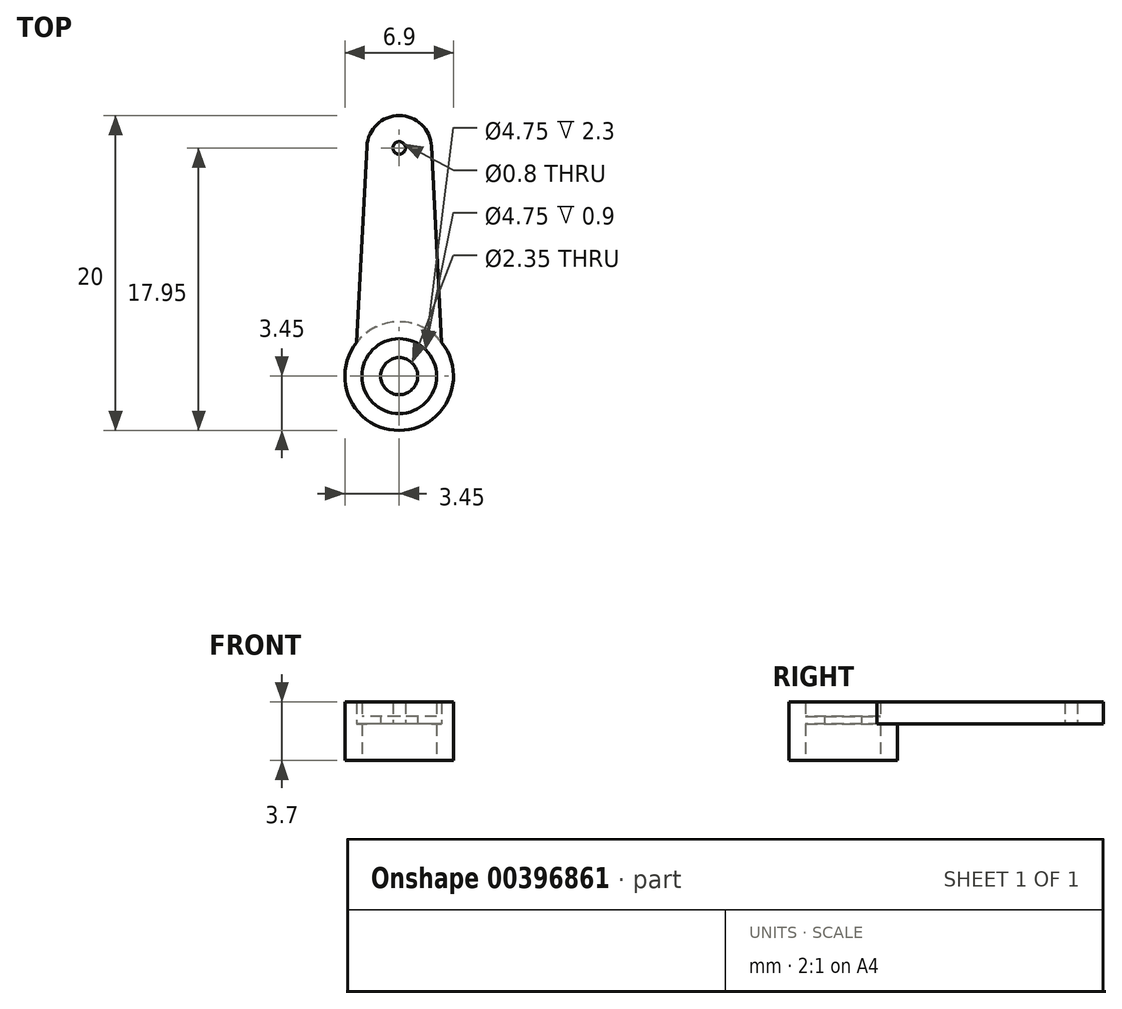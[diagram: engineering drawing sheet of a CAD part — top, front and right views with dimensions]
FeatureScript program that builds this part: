
annotation { "Feature Type Name" : "Feature", "Feature Type Description" : "" }
export const myFeature = defineFeature(function(context is Context, id is Id, definition is map)
    precondition{}
    {
        {
            var Q0;
            Q0=qCreatedBy(makeId("Top.planeOp"),FACE);
            var sketch = newSketch(context, id + "F0", { "sketchPlane" : qUnion([Q0])});
            skCircle(sketch, "E0", {"center": v(0, 0) * mm, "radius": 3.45 * mm});
            skCircle(sketch, "E1", {"center": v(0, 0) * mm, "radius": 2.38 * mm});
            skCircle(sketch, "E2", {"center": v(0, 0) * mm, "radius": 1.18 * mm});
            skCircle(sketch, "E3", {"center": v(0, 14.5) * mm, "radius": 0.4 * mm});
            skCircle(sketch, "E4", {"center": v(0, 14.5) * mm, "radius": 2.05 * mm});
            skLineSegment(sketch, "E5", {"start": v(-2.7, 2.15) * mm, "end": v(-2.05, 14.6) * mm});
            skLineSegment(sketch, "E6", {"start": v(2.05, 14.6) * mm, "end": v(2.7, 2.15) * mm});
            skLineSegment(sketch, "E7", {"start": v(-2.7, 2.15) * mm, "end": v(2.7, 2.15) * mm});
            skLineSegment(sketch, "E8", {"start": v(0, 2.15) * mm, "end": v(0, 0) * mm});
            skSolve(sketch);
        }
        {
            var Q0;
            Q0 = qSketchRegion(id + "F0", true);
            extrude(context, id + "F1", {"entities" : qUnion([Q0]), "depth" : 1.4 * mm});
        }
        {
            var Q0;
            {var subQ0=sQuery(id+"F0.wireOp",EDGE,"E7");var subQ4=sQuery(id+"F0.wireOp",EDGE,"E1");var subQ5=makeQuery(id+"F0.imprint","INTERSECT",VERTEX,{"disambiguationData":[OD(0.0)],"derivedFrom":[subQ4,subQ0]});Q0=makeQuery(id+"F0.imprint","IMPRINT",FACE,{"disambiguationData":[TD([[makeQuery(id+"F0.imprint","IMPRINT",EDGE,{"disambiguationData":[TD([[subQ5,-1.0]])],"derivedFrom":subQ4}),-1.0]])]});}
            var Q1;
            {var subQ0=sQuery(id+"F0.wireOp",EDGE,"E7");var subQ4=sQuery(id+"F0.wireOp",EDGE,"E1");var subQ5=makeQuery(id+"F0.imprint","INTERSECT",VERTEX,{"disambiguationData":[OD(0.0)],"derivedFrom":[subQ4,subQ0]});Q1=makeQuery(id+"F0.imprint","IMPRINT",FACE,{"disambiguationData":[TD([[makeQuery(id+"F0.imprint","IMPRINT",EDGE,{"disambiguationData":[TD([[subQ5,1.0]])],"derivedFrom":subQ4}),-1.0]])]});}
            extrude(context, id + "F2", {"entities" : qUnion([Q0, Q1]), "operationType" : NewBodyOperationType.ADD, "oppositeDirection" : true, "depth" : 2.3 * mm});
        }
        {
            var Q0;
            Q0=makeQuery(id+"F0.imprint","IMPRINT",FACE,{"disambiguationData":[TD([[makeQuery(id+"F0.imprint","IMPRINT",EDGE,{"derivedFrom":sQuery(id+"F0.wireOp",EDGE,"E2")}),-1.0]])]});
            var Q1;
            {var subQ0=sQuery(id+"F0.wireOp",EDGE,"E7");var subQ4=makeQuery(id+"F0.imprint","IMPRINT",VERTEX,{"derivedFrom":subQ0});Q1=makeQuery(id+"F0.imprint","IMPRINT",FACE,{"disambiguationData":[TD([[makeQuery(id+"F0.imprint","IMPRINT",EDGE,{"disambiguationData":[TD([[subQ4,1.0]])],"derivedFrom":subQ0}),1.0]])]});}
            extrude(context, id + "F3", {"entities" : qUnion([Q0, Q1]), "operationType" : NewBodyOperationType.ADD, "depth" : .5 * mm});
        }
    });
